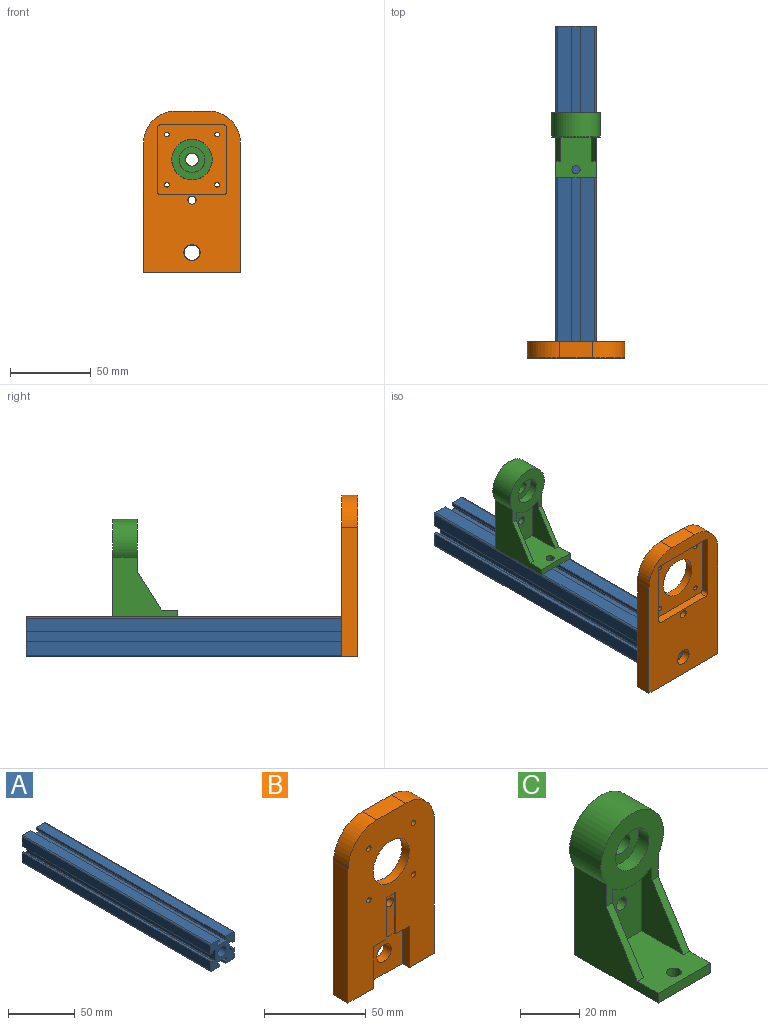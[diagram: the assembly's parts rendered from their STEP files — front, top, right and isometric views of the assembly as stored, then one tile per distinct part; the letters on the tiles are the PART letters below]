
ASSEMBLY  parts=3 mates=5
PART A: 43 faces, bbox 25x200x25 mm
  f0: plane 200x3mm, normal (-1,0,0), area 600mm2, adj f1,f39,f41,f42
  f1: plane 200x2mm, normal (0,0,1), area 400mm2, adj f0,f2,f41,f42
  f2: plane 200x2mm, normal (-1,0,0), area 400mm2, adj f1,f3,f41,f42
  f3: plane 200x8.5mm, normal (0,0,-1), area 1700mm2, adj f2,f4,f41,f42
  f4: cylinder r=1mm len=200mm, axis (0,1,0), area 314.2mm2, adj f3,f5,f41,f42
  f5: plane 200x8.5mm, normal (1,0,0), area 1700mm2, adj f4,f6,f41,f42
  f6: plane 200x2mm, normal (0,0,1), area 400mm2, adj f5,f7,f41,f42
  f7: plane 200x2mm, normal (-1,0,0), area 400mm2, adj f6,f8,f41,f42
  f8: plane 200x3mm, normal (0,0,1), area 600mm2, adj f7,f9,f41,f42
  f9: plane 200x10mm, normal (1,0,0), area 2000mm2, adj f8,f10,f41,f42
  f10: plane 200x3mm, normal (0,0,-1), area 600mm2, adj f9,f11,f41,f42
  f11: plane 200x2mm, normal (-1,0,0), area 400mm2, adj f10,f12,f41,f42
  f12: plane 200x2mm, normal (0,0,-1), area 400mm2, adj f11,f13,f41,f42
  f13: plane 200x8.5mm, normal (1,0,0), area 1700mm2, adj f12,f14,f41,f42
  f14: cylinder r=1mm len=200mm, axis (0,1,0), area 314.2mm2, adj f13,f15,f41,f42
  f15: plane 200x8.5mm, normal (0,0,1), area 1700mm2, adj f14,f16,f41,f42
  f16: plane 200x2mm, normal (-1,0,0), area 400mm2, adj f15,f17,f41,f42
  f17: plane 200x2mm, normal (0,0,-1), area 400mm2, adj f16,f18,f41,f42
  f18: plane 200x3mm, normal (-1,0,0), area 600mm2, adj f17,f19,f41,f42
  f19: plane 200x10mm, normal (0,0,1), area 2000mm2, adj f18,f20,f41,f42
  f20: plane 200x3mm, normal (1,0,0), area 600mm2, adj f19,f21,f41,f42
  f21: plane 200x2mm, normal (0,0,-1), area 400mm2, adj f20,f22,f41,f42
  f22: plane 200x2mm, normal (1,0,0), area 400mm2, adj f21,f23,f41,f42
  f23: plane 200x8.5mm, normal (0,0,1), area 1700mm2, adj f22,f24,f41,f42
  f24: cylinder r=1mm len=200mm, axis (0,1,0), area 314.2mm2, adj f23,f25,f41,f42
  f25: plane 200x8.5mm, normal (-1,0,0), area 1700mm2, adj f24,f26,f41,f42
  f26: plane 200x2mm, normal (0,0,-1), area 400mm2, adj f25,f27,f41,f42
  f27: plane 200x2mm, normal (1,0,0), area 400mm2, adj f26,f28,f41,f42
  f28: plane 200x3mm, normal (0,0,-1), area 600mm2, adj f27,f29,f41,f42
  f29: plane 200x10mm, normal (-1,0,0), area 2000mm2, adj f28,f30,f41,f42
  f30: plane 200x3mm, normal (0,0,1), area 600mm2, adj f29,f31,f41,f42
  f31: plane 200x2mm, normal (1,0,0), area 400mm2, adj f30,f32,f41,f42
  f32: plane 200x2mm, normal (0,0,1), area 400mm2, adj f31,f33,f41,f42
  f33: plane 200x8.5mm, normal (-1,0,0), area 1700mm2, adj f32,f34,f41,f42
  f34: cylinder r=1mm len=200mm, axis (0,1,0), area 314.2mm2, adj f33,f35,f41,f42
  f35: plane 200x8.5mm, normal (0,0,-1), area 1700mm2, adj f34,f36,f41,f42
  f36: plane 200x2mm, normal (1,0,0), area 400mm2, adj f35,f37,f41,f42
  f37: plane 200x2mm, normal (0,0,1), area 400mm2, adj f36,f38,f41,f42
  f38: plane 200x3mm, normal (1,0,0), area 600mm2, adj f37,f39,f41,f42
  f39: plane 200x10mm, normal (0,0,-1), area 2000mm2, adj f0,f38,f41,f42
  f40: cylinder r=4.75mm len=200mm, axis (0,1,0), area 5969mm2, adj f41,f42
  f41: plane 25x25mm, normal (0,-1,0), area 385.3mm2, adj f0,f1,f2,f3,f4,f5,f6,f7
  f42: plane 25x25mm, normal (0,1,0), area 385.3mm2, adj f0,f1,f2,f3,f4,f5,f6,f7
PART B: 32 faces, bbox 60x10x100 mm
  f0: cylinder r=12.5mm len=25mm, axis (0,-1,0), area 392.7mm2, adj f17,f23
  f1: cylinder r=1.5mm len=5mm, axis (0,-1,0), area 47.1mm2, adj f17,f23
  f2: cylinder r=1.5mm len=5mm, axis (0,-1,0), area 47.1mm2, adj f17,f23
  f3: cylinder r=1.5mm len=5mm, axis (0,-1,0), area 47.1mm2, adj f17,f23
  f4: cylinder r=1.5mm len=5mm, axis (0,-1,0), area 47.1mm2, adj f17,f23
  f5: plane 25x5mm, normal (0,0,-1), area 119mm2, adj f7,f15,f16,f17,f19,f21,f22
  f6: cylinder r=2.5mm len=9mm, axis (0,1,0), area 141.4mm2, adj f14,f22
  f7: plane 25x25mm, normal (0,-1,0), area 546.5mm2, adj f5,f9,f15,f16,f18
  f8: plane 80x10mm, normal (-1,0,0), area 800mm2, adj f9,f13,f14,f17
  f9: plane 60x10mm, normal (0,0,-1), area 475mm2, adj f7,f8,f10,f14,f15,f16,f17
  f10: plane 80x10mm, normal (1,0,0), area 800mm2, adj f9,f11,f14,f17
  f11: cylinder r=20mm len=20mm, axis (0,1,0), area 314.2mm2, adj f10,f12,f14,f17
  f12: plane 20x10mm, normal (0,0,1), area 200mm2, adj f11,f13,f14,f17
  f13: cylinder r=20mm len=20mm, axis (0,1,0), area 314.2mm2, adj f8,f12,f14,f17
  f14: plane 100x60mm, normal (0,1,0), area 3884.6mm2, adj f6,f8,f9,f10,f11,f12,f13,f18
  f15: plane 25x5mm, normal (-1,0,0), area 125mm2, adj f5,f7,f9,f17
  f16: plane 25x5mm, normal (1,0,0), area 125mm2, adj f5,f7,f9,f17
  f17: plane 100x60mm, normal (0,-1,0), area 4534.2mm2, adj f0,f1,f2,f3,f4,f5,f8,f9
  f18: cylinder r=5mm len=10mm, axis (0,1,0), area 157.1mm2, adj f7,f14
  f19: plane 25x1mm, normal (-1,0,0), area 25mm2, adj f5,f17,f20,f22
  f20: plane 6x1mm, normal (0,0,-1), area 6mm2, adj f17,f19,f21,f22
  f21: plane 25x1mm, normal (1,0,0), area 25mm2, adj f5,f17,f20,f22
  f22: plane 25x6mm, normal (0,-1,0), area 130.4mm2, adj f5,f6,f19,f20,f21
  f23: plane 43x43mm, normal (0,1,0), area 1326.4mm2, adj f0,f1,f2,f3,f4,f24,f25,f26
  f24: plane 39x5mm, normal (1,0,0), area 195mm2, adj f14,f23,f25,f31
  f25: cylinder r=2mm len=5mm, axis (0,1,0), area 15.7mm2, adj f14,f23,f24,f26
  f26: plane 39x5mm, normal (0,0,-1), area 195mm2, adj f14,f23,f25,f27
  f27: cylinder r=2mm len=5mm, axis (0,1,0), area 15.7mm2, adj f14,f23,f26,f28
  f28: plane 39x5mm, normal (-1,0,0), area 195mm2, adj f14,f23,f27,f29
  f29: cylinder r=2mm len=5mm, axis (0,1,0), area 15.7mm2, adj f14,f23,f28,f30
  f30: plane 39x5mm, normal (0,0,1), area 195mm2, adj f14,f23,f29,f31
  f31: cylinder r=2mm len=5mm, axis (0,1,0), area 15.7mm2, adj f14,f23,f24,f30
PART C: 25 faces, bbox 30x40x60 mm
  f0: plane 40x25mm, normal (0,0,-1), area 974.4mm2, adj f2,f4,f5,f10,f20,f21,f23,f24
  f1: cylinder r=2.5mm len=9mm, axis (0,-1,0), area 141.4mm2, adj f11,f20
  f2: plane 40x36.71mm, normal (1,0,0), area 827.7mm2, adj f0,f3,f5,f9,f10,f12,f13
  f3: cylinder r=15mm len=30mm, axis (0,1,0), area 970.4mm2, adj f2,f4,f5,f13
  f4: plane 40x36.71mm, normal (-1,0,0), area 827.7mm2, adj f0,f3,f5,f9,f10,f13,f14
  f5: plane 60x30mm, normal (0,1,0), area 1155.5mm2, adj f0,f2,f3,f4,f17,f21,f22,f23
  f6: plane 29.39x20mm, normal (1,0,0), area 324.1mm2, adj f7,f9,f11,f13,f14
  f7: cylinder r=15mm len=19mm, axis (0,1,0), area 102.9mm2, adj f6,f8,f11,f13
  f8: plane 29.39x20mm, normal (-1,0,0), area 324.1mm2, adj f7,f9,f11,f12,f13
  f9: plane 30x25mm, normal (0,0,1), area 610.4mm2, adj f2,f4,f6,f8,f10,f11,f12,f14
  f10: plane 25x4mm, normal (0,-1,0), area 100mm2, adj f0,f2,f4,f9
  f11: plane 29.39x19mm, normal (0,-1,0), area 494.8mm2, adj f1,f6,f7,f8,f9
  f12: plane 23.61x15mm, normal (0,-0.84,0.54), area 83.9mm2, adj f2,f8,f9,f13
  f13: plane 32.39x30mm, normal (0,-1,0), area 549.4mm2, adj f2,f3,f4,f6,f7,f8,f12,f14
  f14: plane 23.61x15mm, normal (0,-0.84,0.54), area 83.9mm2, adj f4,f6,f9,f13
  f15: plane 16x16mm, normal (0,-1,0), area 150.8mm2, adj f16,f19
  f16: cylinder r=8mm len=16mm, axis (0,1,0), area 251.3mm2, adj f13,f15
  f17: cylinder r=8mm len=16mm, axis (0,1,0), area 251.3mm2, adj f5,f18
  f18: plane 16x16mm, normal (0,1,0), area 150.8mm2, adj f17,f19
  f19: cylinder r=4mm len=8mm, axis (0,-1,0), area 125.7mm2, adj f15,f18
  f20: plane 25x6mm, normal (0,1,0), area 130.4mm2, adj f0,f1,f21,f22,f23
  f21: plane 25x1mm, normal (1,0,0), area 25mm2, adj f0,f5,f20,f22
  f22: plane 6x1mm, normal (0,0,-1), area 6mm2, adj f5,f20,f21,f23
  f23: plane 25x1mm, normal (-1,0,0), area 25mm2, adj f0,f5,f20,f22
  f24: cylinder r=2.5mm len=5mm, axis (0,0,1), area 62.8mm2, adj f0,f9
PLACE A t=(-133.95,102.02,-26.6)mm
PLACE B rot(axis=(0,0,1),180deg) t=(-133.95,-102.98,-39.1)mm
PLACE C t=(-133.95,48.38,-14.1)mm
MATE planar B.f18 <-> A.f41  axis (0,1,0) through (-133.95,-97.98,-26.6)mm
MATE planar B.f16 <-> A.f13  axis (-1,0,0) through (-121.45,-95.48,-26.6)mm
MATE planar C.f2 <-> A.f5  axis (1,0,0) through (-121.45,35.79,0.89)mm
MATE slider B.f18 <-> A.f40  axis (0,-1,0) through (-133.95,-102.98,-26.6)mm
MATE planar A.f15 <-> C.f0  axis (0,0,1) through (-126.7,2.02,-14.1)mm
